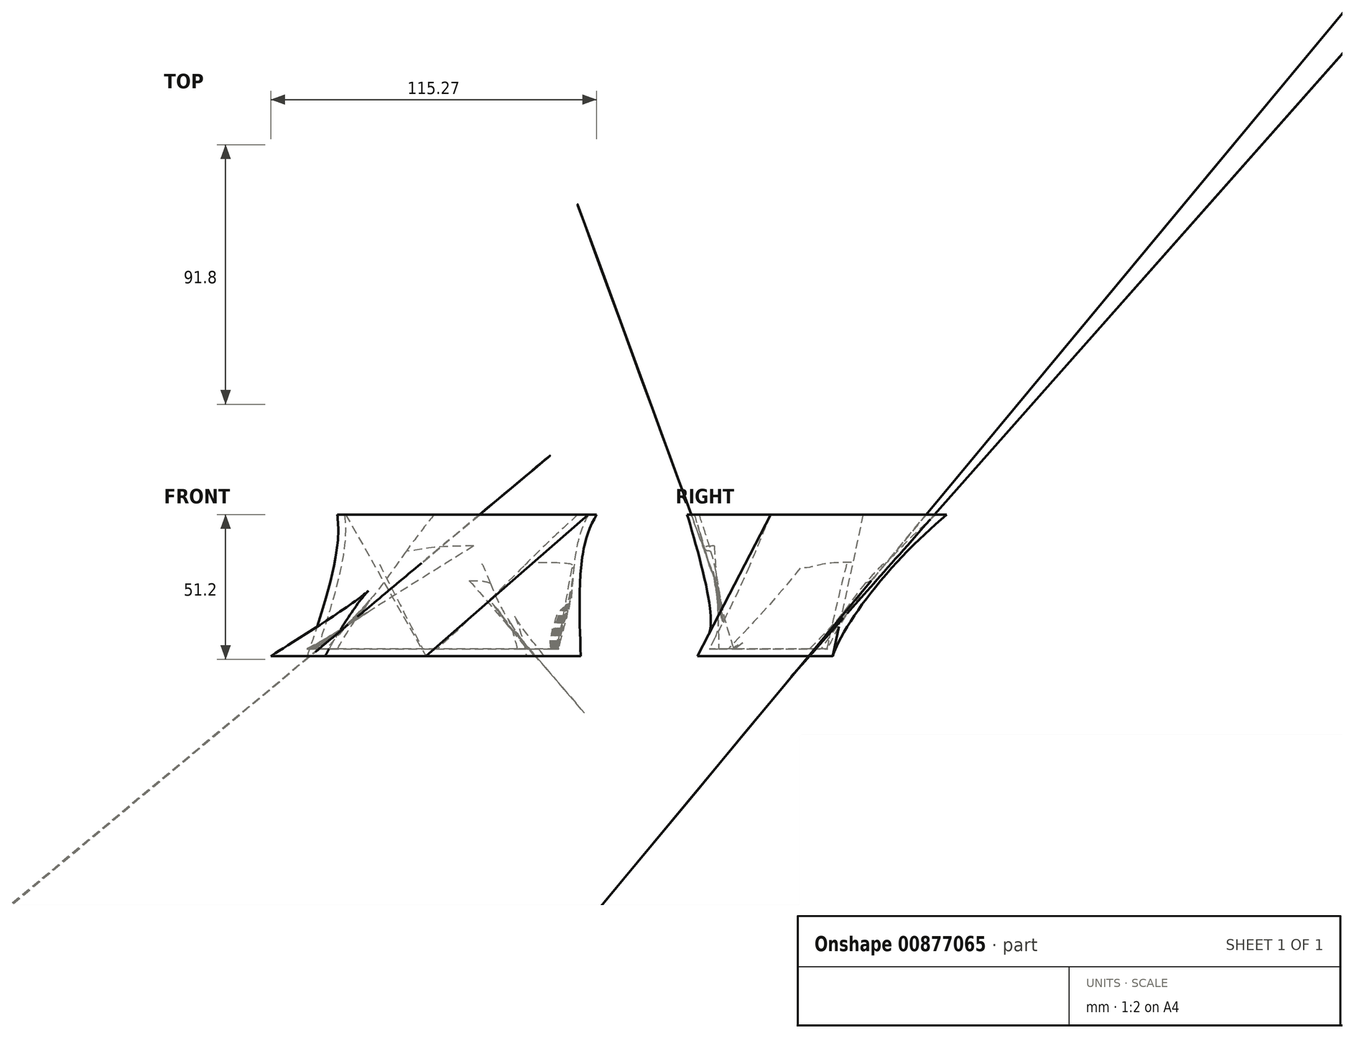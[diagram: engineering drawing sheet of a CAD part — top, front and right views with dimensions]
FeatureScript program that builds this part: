
annotation { "Feature Type Name" : "Feature", "Feature Type Description" : "" }
export const myFeature = defineFeature(function(context is Context, id is Id, definition is map)
    precondition{}
    {
        {
            var Q0;
            Q0=qCreatedBy(makeId("Top.planeOp"),FACE);
            var sketch = newSketch(context, id + "F0", { "sketchPlane" : qUnion([Q0])});
            skFitSpline(sketch, "E0", {"points": [v(0, 47.8) * mm, v(41.84, 40.59) * mm, v(36.06, 19.9) * mm, v(54.63, 8.82) * mm, v(0, 0) * mm], "startDerivative": vector(218.26, 1.82) * mm, "endDerivative": vector(-269.64, -24.04) * mm});
            skFitSpline(sketch, "E1.MirrorCS", {"points": [v(0, 47.8) * mm, v(-41.84, 40.59) * mm, v(-36.06, 19.9) * mm, v(-54.63, 8.82) * mm, v(0, 0) * mm], "startDerivative": vector(-218.26, 1.82) * mm, "endDerivative": vector(269.64, -24.04) * mm});
            skSolve(sketch);
        }
        {
            var Q0;
            Q0=qCreatedBy(makeId("Top.planeOp"),FACE);
            cPlane(context, id + "F1", {"entities" : qUnion([Q0]), "cplaneType" : CPlaneType.OFFSET, "offset" : 50 * mm, "width" : 152.4 * mm, "height" : 152.4 * mm});
        }
        {
            var Q0;
            Q0=qCreatedBy(id+"F1.planeOp",FACE);
            var sketch = newSketch(context, id + "F2", { "sketchPlane" : qUnion([Q0])});
            skCircle(sketch, "E2", {"center": v(14.54, 42.27) * mm, "radius": 45.9 * mm});
            skSolve(sketch);
        }
        {
            var Q0;
            Q0=makeQuery(id+"F2.imprint","IMPRINT",FACE,{"disambiguationData":[TD([[makeQuery(id+"F2.imprint","IMPRINT",EDGE,{"derivedFrom":sQuery(id+"F2.wireOp",EDGE,"E2")}),1.0]])]});
            var Q1;
            Q1=makeQuery(id+"F0.imprint","IMPRINT",FACE,{"disambiguationData":[TD([[makeQuery(id+"F0.imprint","IMPRINT",EDGE,{"derivedFrom":sQuery(id+"F0.wireOp",EDGE,"E0")}),-1.0]])]});
            loft(context, id + "F3", {"sheetProfilesArray" : [{ "sheetProfileEntities" : qUnion([Q0]) }, { "sheetProfileEntities" : qUnion([Q1]) }]});
        }
        {
            var Q0;
            Q0=makeQuery(id+"F3.opLoft","CAP_FACE",FACE,{"disambiguationData":[OSD([makeQuery(id+"F2.imprint","IMPRINT",FACE,{"disambiguationData":[TD([[makeQuery(id+"F2.imprint","IMPRINT",EDGE,{"derivedFrom":sQuery(id+"F2.wireOp",EDGE,"E2")}),1.0]])]})])],"isStart":true});
            shell(context, id + "F4", {"entities" : qUnion([Q0]), "thickness" : 2.54 * mm});
        }
    });
